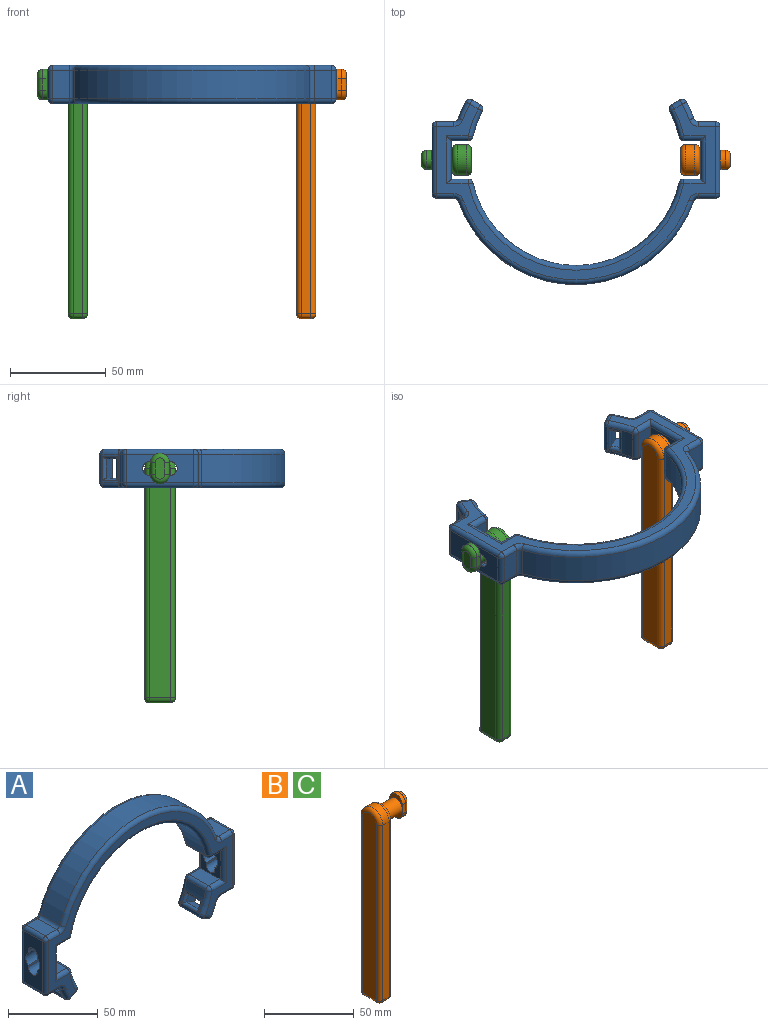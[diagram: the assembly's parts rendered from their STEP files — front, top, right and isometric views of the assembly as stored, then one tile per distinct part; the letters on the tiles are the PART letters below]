
ASSEMBLY  parts=3 mates=1
PART A: 150 faces, bbox 150x20x101.9 mm
  f0: cylinder r=55mm len=15mm, axis (0,-1,0), area 115.1mm2, adj f43,f44,f54,f55,f75,f76,f78
  f1: plane 15x8.86mm, normal (0,0,-1), area 132.9mm2, adj f57,f58,f66,f67
  f2: cylinder r=55mm len=107.37mm, axis (0,-1,0), area 2230.2mm2, adj f25,f28,f29,f102
  f3: plane 145x91.56mm, normal (0,1,0), area 1476.3mm2, adj f25,f27,f30,f31,f33,f34,f38,f43
  f4: plane 145x91.56mm, normal (0,-1,0), area 1476.3mm2, adj f29,f35,f36,f40,f41,f45,f46,f55
  f5: cylinder r=65mm len=122.57mm, axis (0,-1,0), area 2400.4mm2, adj f30,f36,f37,f108
  f6: plane 15x8.86mm, normal (0,0,1), area 132.9mm2, adj f37,f38,f46,f47
  f7: plane 15x8.88mm, normal (0,0,-1), area 133.1mm2, adj f8,f27,f28,f35
  f8: plane 20x15mm, normal (-1,0,0), area 160.9mm2, adj f7,f9,f11,f12,f13,f14,f15,f16
  f9: plane 15x8.88mm, normal (0,0,1), area 133.1mm2, adj f8,f34,f44,f45
  f10: plane 35x15mm, normal (1,0,0), area 385.9mm2, adj f11,f12,f13,f14,f15,f16,f17,f18
  f11: plane 10x1.26mm, normal (0,-1,0), area 12.6mm2, adj f8,f10,f12,f18
  f12: cylinder r=5.5mm len=10mm, axis (1,0,0), area 96.9mm2, adj f8,f10,f11,f13
  f13: plane 10x1.26mm, normal (0,-1,0), area 12.6mm2, adj f8,f10,f12,f14
  f14: cylinder r=3.5mm len=10mm, axis (1,0,0), area 110mm2, adj f8,f10,f13,f15
  f15: plane 10x1.26mm, normal (0,1,0), area 12.6mm2, adj f8,f10,f14,f16
  f16: cylinder r=5.5mm len=10mm, axis (1,0,0), area 96.9mm2, adj f8,f10,f15,f17
  f17: plane 10x1.26mm, normal (0,1,0), area 12.6mm2, adj f8,f10,f16,f18
  f18: cylinder r=3.5mm len=10mm, axis (1,0,0), area 110mm2, adj f8,f10,f11,f17
  f19: plane 15x4.33mm, normal (-0.5,0,-0.87), area 75.1mm2, adj f53,f54,f64,f65
  f20: cylinder r=65mm len=15mm, axis (0,-1,0), area 26.5mm2, adj f59,f64,f67,f70,f71,f72,f73,f74
  f21: plane 8.5x7.59mm, normal (0,-1,0), area 36.7mm2, adj f23,f24,f72,f73,f74,f78
  f22: plane 8.5x7.59mm, normal (0,1,0), area 36.7mm2, adj f23,f24,f71,f72,f73,f75
  f23: plane 10x6.54mm, normal (-0.36,0,-0.93), area 70mm2, adj f21,f22,f72,f75,f76,f78
  f24: plane 10x6.29mm, normal (0.44,0,0.9), area 70mm2, adj f21,f22,f73,f75,f77,f78
  f25: torus R=57.5mm, axis (0,-1,0), area 593.5mm2, adj f2,f3,f26,f100
  f26: sphere r=2.5mm, area 8.4mm2, adj f25,f27,f28
  f27: cylinder r=2.5mm len=11.38mm, axis (-1,0,0), area 38.4mm2, adj f3,f7,f26,f31
  f28: cylinder r=2.5mm len=15mm, axis (0,-1,0), area 50.7mm2, adj f2,f7,f26,f32
  f29: torus R=57.5mm, axis (0,-1,0), area 593.5mm2, adj f2,f4,f32,f104
  f30: torus R=62.5mm, axis (0,-1,0), area 619.6mm2, adj f3,f5,f33,f105
  f31: cylinder r=2.5mm len=25mm, axis (0,0,1), area 85.7mm2, adj f3,f8,f27,f34
  f32: sphere r=2.5mm, area 8.4mm2, adj f28,f29,f35
  f33: torus R=5mm, axis (0,-1,0), area 16.5mm2, adj f3,f30,f37,f38
  f34: cylinder r=2.5mm len=11.38mm, axis (1,0,0), area 38.4mm2, adj f3,f9,f31,f39
  f35: cylinder r=2.5mm len=11.38mm, axis (1,0,0), area 38.4mm2, adj f4,f7,f32,f40
  f36: torus R=62.5mm, axis (0,-1,0), area 619.6mm2, adj f4,f5,f41,f112
  f37: cylinder r=2.5mm len=15mm, axis (0,-1,0), area 46.2mm2, adj f5,f6,f33,f41
  f38: cylinder r=2.5mm len=8.86mm, axis (1,0,0), area 34.8mm2, adj f3,f6,f33,f42
  f39: sphere r=2.5mm, area 8.4mm2, adj f34,f43,f44
  f40: cylinder r=2.5mm len=25mm, axis (0,0,-1), area 85.7mm2, adj f4,f8,f35,f45
  f41: torus R=5mm, axis (0,-1,0), area 16.5mm2, adj f4,f36,f37,f46
  f42: sphere r=2.5mm, area 9.8mm2, adj f38,f47,f48
  f43: torus R=57.5mm, axis (0,-1,0), area 57.3mm2, adj f0,f3,f39,f49
  f44: cylinder r=2.5mm len=15mm, axis (0,-1,0), area 50.7mm2, adj f0,f9,f39,f50
  f45: cylinder r=2.5mm len=11.38mm, axis (-1,0,0), area 38.4mm2, adj f4,f9,f40,f50
  f46: cylinder r=2.5mm len=8.86mm, axis (-1,0,0), area 34.8mm2, adj f4,f6,f41,f51
  f47: cylinder r=2.5mm len=15mm, axis (0,-1,0), area 58.9mm2, adj f6,f10,f42,f51
  f48: cylinder r=2.5mm len=35mm, axis (0,0,-1), area 137.4mm2, adj f3,f10,f42,f52
  f49: sphere r=2.5mm, area 9.5mm2, adj f43,f53,f54
  f50: sphere r=2.5mm, area 8.4mm2, adj f44,f45,f55
  f51: sphere r=2.5mm, area 9.8mm2, adj f46,f47,f56
  f52: sphere r=2.5mm, area 9.8mm2, adj f48,f57,f58
  f53: cylinder r=2.5mm len=5.58mm, axis (-0.87,0,0.5), area 19.7mm2, adj f3,f19,f49,f60
  f54: cylinder r=2.5mm len=15mm, axis (0,-1,0), area 57.2mm2, adj f0,f19,f49,f61,f75,f77,f78
  f55: torus R=57.5mm, axis (0,-1,0), area 57.3mm2, adj f0,f4,f50,f61
  f56: cylinder r=2.5mm len=35mm, axis (0,0,1), area 137.4mm2, adj f4,f10,f51,f62
  f57: cylinder r=2.5mm len=15mm, axis (0,1,0), area 58.9mm2, adj f1,f10,f52,f62
  f58: cylinder r=2.5mm len=8.86mm, axis (-1,0,0), area 34.8mm2, adj f1,f3,f52,f63
  f59: torus R=62.5mm, axis (0,-1,0), area 36.2mm2, adj f3,f20,f60,f63
  f60: sphere r=2.5mm, area 10.1mm2, adj f53,f59,f64
  f61: sphere r=2.5mm, area 9.5mm2, adj f54,f55,f65
  f62: sphere r=2.5mm, area 9.8mm2, adj f56,f57,f66
  f63: torus R=5mm, axis (0,-1,0), area 16.5mm2, adj f3,f58,f59,f67
  f64: cylinder r=2.5mm len=15mm, axis (0,-1,0), area 60.4mm2, adj f19,f20,f60,f68
  f65: cylinder r=2.5mm len=5.58mm, axis (0.87,0,-0.5), area 19.7mm2, adj f4,f19,f61,f68
  f66: cylinder r=2.5mm len=8.86mm, axis (1,0,0), area 34.8mm2, adj f1,f4,f62,f69
  f67: cylinder r=2.5mm len=15mm, axis (0,-1,0), area 46.2mm2, adj f1,f20,f63,f69
  f68: sphere r=2.5mm, area 10.1mm2, adj f64,f65,f70
  f69: torus R=5mm, axis (0,-1,0), area 16.5mm2, adj f4,f66,f67,f70
  f70: torus R=62.5mm, axis (0,-1,0), area 36.2mm2, adj f4,f20,f68,f69
  f71: torus R=63.5mm, axis (0,-1,0), area 15.9mm2, adj f20,f22,f72,f73
  f72: cylinder r=1.5mm len=13mm, axis (0,-1,0), area 26.5mm2, adj f20,f21,f22,f23,f71,f74
  f73: cylinder r=1.5mm len=13mm, axis (0,-1,0), area 26.5mm2, adj f20,f21,f22,f24,f71,f74
  f74: torus R=63.5mm, axis (0,-1,0), area 15.9mm2, adj f20,f21,f72,f73
  f75: torus R=56.5mm, axis (0,-1,0), area 13.9mm2, adj f0,f22,f23,f24,f54,f76,f77
  f76: cylinder r=1.5mm len=13mm, axis (0,-1,0), area 25.7mm2, adj f0,f23,f75,f78
  f77: cylinder r=1.5mm len=12.99mm, axis (0,-1,0), area 25.6mm2, adj f24,f54,f75,f78
  f78: torus R=56.5mm, axis (0,-1,0), area 13.9mm2, adj f0,f21,f23,f24,f54,f76,f77
  f79: cylinder r=55mm len=15mm, axis (0,-1,0), area 115.1mm2, adj f114,f115,f125,f126,f146,f147,f149
  f80: plane 15x8.86mm, normal (0,0,-1), area 132.9mm2, adj f128,f129,f137,f138
  f81: plane 15x8.86mm, normal (0,0,1), area 132.9mm2, adj f108,f109,f117,f118
  f82: plane 15x8.88mm, normal (0,0,-1), area 133.1mm2, adj f83,f101,f102,f107
  f83: plane 20x15mm, normal (1,0,0), area 160.9mm2, adj f82,f84,f86,f87,f88,f89,f90,f91
  f84: plane 15x8.88mm, normal (0,0,1), area 133.1mm2, adj f83,f106,f115,f116
  f85: plane 35x15mm, normal (-1,0,0), area 385.9mm2, adj f86,f87,f88,f89,f90,f91,f92,f93
  f86: plane 10x1.26mm, normal (0,-1,0), area 12.6mm2, adj f83,f85,f87,f93
  f87: cylinder r=5.5mm len=10mm, axis (-1,0,0), area 96.9mm2, adj f83,f85,f86,f88
  f88: plane 10x1.26mm, normal (0,-1,0), area 12.6mm2, adj f83,f85,f87,f89
  f89: cylinder r=3.5mm len=10mm, axis (-1,0,0), area 110mm2, adj f83,f85,f88,f90
  f90: plane 10x1.26mm, normal (0,1,0), area 12.6mm2, adj f83,f85,f89,f91
  f91: cylinder r=5.5mm len=10mm, axis (-1,0,0), area 96.9mm2, adj f83,f85,f90,f92
  f92: plane 10x1.26mm, normal (0,1,0), area 12.6mm2, adj f83,f85,f91,f93
  f93: cylinder r=3.5mm len=10mm, axis (-1,0,0), area 110mm2, adj f83,f85,f86,f92
  f94: plane 15x4.33mm, normal (0.5,0,-0.87), area 75.1mm2, adj f124,f125,f135,f136
  f95: cylinder r=65mm len=15mm, axis (0,-1,0), area 26.5mm2, adj f130,f135,f138,f141,f142,f143,f144,f145
  f96: plane 8.5x7.59mm, normal (0,-1,0), area 36.7mm2, adj f98,f99,f143,f144,f145,f149
  f97: plane 8.5x7.59mm, normal (0,1,0), area 36.7mm2, adj f98,f99,f142,f143,f144,f146
  f98: plane 10x6.54mm, normal (0.36,0,-0.93), area 70mm2, adj f96,f97,f143,f146,f147,f149
  f99: plane 10x6.29mm, normal (-0.44,0,0.9), area 70mm2, adj f96,f97,f144,f146,f148,f149
  f100: sphere r=2.5mm, area 8.4mm2, adj f25,f101,f102
  f101: cylinder r=2.5mm len=11.38mm, axis (1,0,0), area 38.4mm2, adj f3,f82,f100,f103
  f102: cylinder r=2.5mm len=15mm, axis (0,-1,0), area 50.7mm2, adj f2,f82,f100,f104
  f103: cylinder r=2.5mm len=25mm, axis (0,0,1), area 85.7mm2, adj f3,f83,f101,f106
  f104: sphere r=2.5mm, area 8.4mm2, adj f29,f102,f107
  f105: torus R=5mm, axis (0,-1,0), area 16.5mm2, adj f3,f30,f108,f109
  f106: cylinder r=2.5mm len=11.38mm, axis (-1,0,0), area 38.4mm2, adj f3,f84,f103,f110
  f107: cylinder r=2.5mm len=11.38mm, axis (-1,0,0), area 38.4mm2, adj f4,f82,f104,f111
  f108: cylinder r=2.5mm len=15mm, axis (0,-1,0), area 46.2mm2, adj f5,f81,f105,f112
  f109: cylinder r=2.5mm len=8.86mm, axis (-1,0,0), area 34.8mm2, adj f3,f81,f105,f113
  f110: sphere r=2.5mm, area 8.4mm2, adj f106,f114,f115
  f111: cylinder r=2.5mm len=25mm, axis (0,0,-1), area 85.7mm2, adj f4,f83,f107,f116
  f112: torus R=5mm, axis (0,-1,0), area 16.5mm2, adj f4,f36,f108,f117
  f113: sphere r=2.5mm, area 9.8mm2, adj f109,f118,f119
  f114: torus R=57.5mm, axis (0,-1,0), area 57.3mm2, adj f3,f79,f110,f120
  f115: cylinder r=2.5mm len=15mm, axis (0,-1,0), area 50.7mm2, adj f79,f84,f110,f121
  f116: cylinder r=2.5mm len=11.38mm, axis (1,0,0), area 38.4mm2, adj f4,f84,f111,f121
  f117: cylinder r=2.5mm len=8.86mm, axis (1,0,0), area 34.8mm2, adj f4,f81,f112,f122
  f118: cylinder r=2.5mm len=15mm, axis (0,-1,0), area 58.9mm2, adj f81,f85,f113,f122
  f119: cylinder r=2.5mm len=35mm, axis (0,0,-1), area 137.4mm2, adj f3,f85,f113,f123
  f120: sphere r=2.5mm, area 9.5mm2, adj f114,f124,f125
  f121: sphere r=2.5mm, area 8.4mm2, adj f115,f116,f126
  f122: sphere r=2.5mm, area 9.8mm2, adj f117,f118,f127
  f123: sphere r=2.5mm, area 9.8mm2, adj f119,f128,f129
  f124: cylinder r=2.5mm len=5.58mm, axis (0.87,0,0.5), area 19.7mm2, adj f3,f94,f120,f131
  f125: cylinder r=2.5mm len=15mm, axis (0,-1,0), area 57.2mm2, adj f79,f94,f120,f132,f146,f148,f149
  f126: torus R=57.5mm, axis (0,-1,0), area 57.3mm2, adj f4,f79,f121,f132
  f127: cylinder r=2.5mm len=35mm, axis (0,0,1), area 137.4mm2, adj f4,f85,f122,f133
  f128: cylinder r=2.5mm len=15mm, axis (0,1,0), area 58.9mm2, adj f80,f85,f123,f133
  f129: cylinder r=2.5mm len=8.86mm, axis (1,0,0), area 34.8mm2, adj f3,f80,f123,f134
  f130: torus R=62.5mm, axis (0,-1,0), area 36.2mm2, adj f3,f95,f131,f134
  f131: sphere r=2.5mm, area 10.1mm2, adj f124,f130,f135
  f132: sphere r=2.5mm, area 9.5mm2, adj f125,f126,f136
  f133: sphere r=2.5mm, area 9.8mm2, adj f127,f128,f137
  f134: torus R=5mm, axis (0,-1,0), area 16.5mm2, adj f3,f129,f130,f138
  f135: cylinder r=2.5mm len=15mm, axis (0,-1,0), area 60.4mm2, adj f94,f95,f131,f139
  f136: cylinder r=2.5mm len=5.58mm, axis (-0.87,0,-0.5), area 19.7mm2, adj f4,f94,f132,f139
  f137: cylinder r=2.5mm len=8.86mm, axis (-1,0,0), area 34.8mm2, adj f4,f80,f133,f140
  f138: cylinder r=2.5mm len=15mm, axis (0,-1,0), area 46.2mm2, adj f80,f95,f134,f140
  f139: sphere r=2.5mm, area 10.1mm2, adj f135,f136,f141
  f140: torus R=5mm, axis (0,-1,0), area 16.5mm2, adj f4,f137,f138,f141
  f141: torus R=62.5mm, axis (0,-1,0), area 36.2mm2, adj f4,f95,f139,f140
  f142: torus R=63.5mm, axis (0,-1,0), area 15.9mm2, adj f95,f97,f143,f144
  f143: cylinder r=1.5mm len=13mm, axis (0,-1,0), area 26.5mm2, adj f95,f96,f97,f98,f142,f145
  f144: cylinder r=1.5mm len=13mm, axis (0,-1,0), area 26.5mm2, adj f95,f96,f97,f99,f142,f145
  f145: torus R=63.5mm, axis (0,-1,0), area 15.9mm2, adj f95,f96,f143,f144
  f146: torus R=56.5mm, axis (0,-1,0), area 13.9mm2, adj f79,f97,f98,f99,f125,f147,f148
  f147: cylinder r=1.5mm len=13mm, axis (0,-1,0), area 25.7mm2, adj f79,f98,f146,f149
  f148: cylinder r=1.5mm len=12.99mm, axis (0,-1,0), area 25.6mm2, adj f99,f125,f146,f149
  f149: torus R=56.5mm, axis (0,-1,0), area 13.9mm2, adj f79,f96,f98,f99,f125,f147,f148
PART B: 32 faces, bbox 26x17.3x130.7 mm
  f0: plane 119.5x5mm, normal (0,-1,0), area 597.5mm2, adj f11,f18,f23,f26
  f1: plane 11x5mm, normal (0,0,-1), area 55mm2, adj f22,f23,f27,f28
  f2: plane 119.5x5mm, normal (0,1,0), area 597.5mm2, adj f11,f21,f27,f31
  f3: plane 125x11mm, normal (1,0,0), area 1283.5mm2, adj f5,f26,f28,f29,f31
  f4: plane 125x11mm, normal (-1,0,0), area 1362mm2, adj f18,f19,f21,f22
  f5: cylinder r=5mm len=11mm, axis (-1,0,0), area 345.6mm2, adj f3,f6,f7
  f6: plane 10x8mm, normal (-1,0,0), area 30mm2, adj f5,f8,f9,f13
  f7: plane 10x8mm, normal (-1,0,0), area 30mm2, adj f5,f8,f9,f12
  f8: plane 6x2.5mm, normal (0,1,0), area 15mm2, adj f6,f7,f12,f13,f16
  f9: plane 6x2.5mm, normal (0,-1,0), area 15mm2, adj f6,f7,f12,f13,f15
  f10: plane 11x5mm, normal (1,0,0), area 49.6mm2, adj f14,f15,f16,f17
  f11: cylinder r=8mm len=16mm, axis (1,0,0), area 125.7mm2, adj f0,f2,f19,f29
  f12: cylinder r=5mm len=10mm, axis (1,0,0), area 39.3mm2, adj f7,f8,f9,f17
  f13: cylinder r=5mm len=10mm, axis (1,0,0), area 39.3mm2, adj f6,f8,f9,f14
  f14: torus R=2.5mm, axis (1,0,0), area 50.5mm2, adj f10,f13,f15,f16
  f15: cylinder r=2.5mm len=6mm, axis (0,0,1), area 23.6mm2, adj f9,f10,f14,f17
  f16: cylinder r=2.5mm len=6mm, axis (0,0,-1), area 23.6mm2, adj f8,f10,f14,f17
  f17: torus R=2.5mm, axis (1,0,0), area 50.5mm2, adj f10,f12,f15,f16
  f18: cylinder r=2.5mm len=119.5mm, axis (0,0,-1), area 469.3mm2, adj f0,f4,f19,f20
  f19: torus R=5.5mm, axis (1,0,0), area 87.5mm2, adj f4,f11,f18,f21
  f20: sphere r=2.5mm, area 9.8mm2, adj f18,f22,f23
  f21: cylinder r=2.5mm len=119.5mm, axis (0,0,1), area 469.3mm2, adj f2,f4,f19,f24
  f22: cylinder r=2.5mm len=11mm, axis (0,1,0), area 43.2mm2, adj f1,f4,f20,f24
  f23: cylinder r=2.5mm len=5mm, axis (-1,0,0), area 19.6mm2, adj f0,f1,f20,f25
  f24: sphere r=2.5mm, area 9.8mm2, adj f21,f22,f27
  f25: sphere r=2.5mm, area 9.8mm2, adj f23,f26,f28
  f26: cylinder r=2.5mm len=119.5mm, axis (0,0,1), area 469.3mm2, adj f0,f3,f25,f29
  f27: cylinder r=2.5mm len=5mm, axis (1,0,0), area 19.6mm2, adj f1,f2,f24,f30
  f28: cylinder r=2.5mm len=11mm, axis (0,-1,0), area 43.2mm2, adj f1,f3,f25,f30
  f29: torus R=5.5mm, axis (1,0,0), area 87.5mm2, adj f3,f11,f26,f31
  f30: sphere r=2.5mm, area 9.8mm2, adj f27,f28,f31
  f31: cylinder r=2.5mm len=119.5mm, axis (0,0,-1), area 469.3mm2, adj f2,f3,f29,f30
PART C: same geometry as B
PLACE A rot(axis=(1,0,0),90deg) t=(0,0,0)mm
PLACE B t=(54.5,0,0)mm
PLACE C rot(axis=(0,0,1),180deg) t=(-54.5,0,0)mm
MATE planar B.f3 <-> A.f87  axis (1,0,0) through (64.5,0,-61.11)mm
